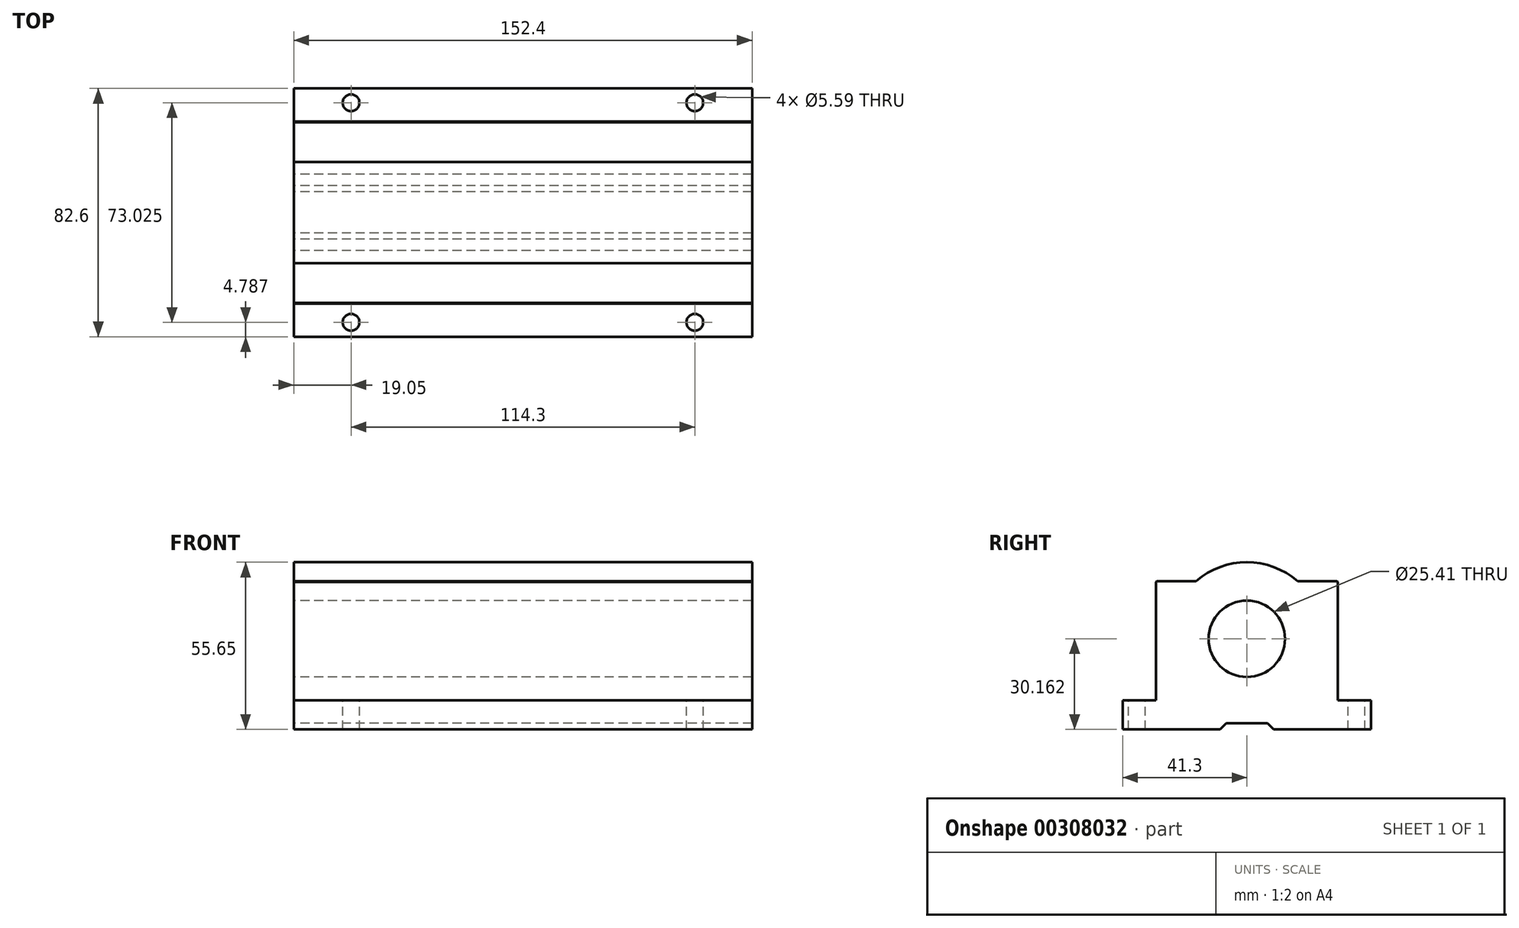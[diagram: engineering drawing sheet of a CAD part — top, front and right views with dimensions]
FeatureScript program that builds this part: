
annotation { "Feature Type Name" : "Feature", "Feature Type Description" : "" }
export const myFeature = defineFeature(function(context is Context, id is Id, definition is map)
    precondition{}
    {
        {
            var Q0;
            Q0=qCreatedBy(makeId("Right.planeOp"),FACE);
            var sketch = newSketch(context, id + "F0", { "sketchPlane" : qUnion([Q0])});
            skCircle(sketch, "E0", {"center": v(0, 3.86) * mm, "radius": 12.7 * mm});
            skLineSegment(sketch, "E1", {"start": v(-8.9, -26.3) * mm, "end": v(-6.86, -24.27) * mm});
            skLineSegment(sketch, "E2", {"start": v(-41.3, -26.3) * mm, "end": v(-8.9, -26.3) * mm});
            skLineSegment(sketch, "E3", {"start": v(-41.3, -16.65) * mm, "end": v(-41.3, -26.3) * mm});
            skLineSegment(sketch, "E4", {"start": v(-29.99, 23) * mm, "end": v(-30.24, 22.74) * mm});
            skLineSegment(sketch, "E5", {"start": v(-30.24, -16.65) * mm, "end": v(-41.3, -16.65) * mm});
            skLineSegment(sketch, "E6", {"start": v(-30.24, 22.74) * mm, "end": v(-30.24, -16.65) * mm});
            skLineSegment(sketch, "E7", {"start": v(-16.86, 23) * mm, "end": v(-29.99, 23) * mm});
            skArc(sketch, "E8", {"start": v(16.86, 23) * mm, "mid": v(0, 29.35) * mm, "end": v(-16.86, 23) * mm});
            skLineSegment(sketch, "E9", {"start": v(29.99, 23) * mm, "end": v(16.86, 23) * mm});
            skLineSegment(sketch, "E10", {"start": v(30.24, -16.65) * mm, "end": v(30.24, 22.74) * mm});
            skLineSegment(sketch, "E11", {"start": v(41.3, -16.65) * mm, "end": v(30.24, -16.65) * mm});
            skLineSegment(sketch, "E12", {"start": v(41.3, -26.3) * mm, "end": v(41.3, -16.65) * mm});
            skLineSegment(sketch, "E13", {"start": v(8.9, -26.3) * mm, "end": v(41.3, -26.3) * mm});
            skLineSegment(sketch, "E14", {"start": v(6.86, -24.27) * mm, "end": v(8.9, -26.3) * mm});
            skLineSegment(sketch, "E15", {"start": v(-6.86, -24.27) * mm, "end": v(6.86, -24.27) * mm});
            skLineSegment(sketch, "E16", {"start": v(30.24, 22.74) * mm, "end": v(29.99, 23) * mm});
            skSolve(sketch);
        }
        {
            var Q0;
            Q0 = qSketchRegion(id + "F0", true);
            extrude(context, id + "F1", {"entities" : qUnion([Q0]), "endBound" : BoundingType.SYMMETRIC, "depth" : 152.4 * mm});
        }
        {
            var Q0;
            Q0=makeQuery(id+"F1.opExtrude","SWEPT_FACE",FACE,{"disambiguationData":[OSD([sQuery(id+"F0.wireOp",EDGE,"E11")])]});
            var sketch = newSketch(context, id + "F2", { "sketchPlane" : qUnion([Q0])});
            skCircle(sketch, "E17", {"center": v(57.15, 36.51) * mm, "radius": 2.8 * mm});
            skCircle(sketch, "E18", {"center": v(-57.15, 36.51) * mm, "radius": 2.8 * mm});
            skCircle(sketch, "E19", {"center": v(-57.15, -36.51) * mm, "radius": 2.8 * mm});
            skCircle(sketch, "E20", {"center": v(57.15, -36.51) * mm, "radius": 2.8 * mm});
            skLineSegment(sketch, "E21", {"start": v(0, 0) * mm, "end": v(13.84, 0) * mm});
            skSolve(sketch);
        }
        {
            var Q0;
            Q0 = qSketchRegion(id + "F2", true);
            extrude(context, id + "F3", {"entities" : qUnion([Q0]), "operationType" : NewBodyOperationType.REMOVE, "endBound" : BoundingType.THROUGH_ALL, "oppositeDirection" : true, "depth" : 25.4 * mm});
        }
    });
